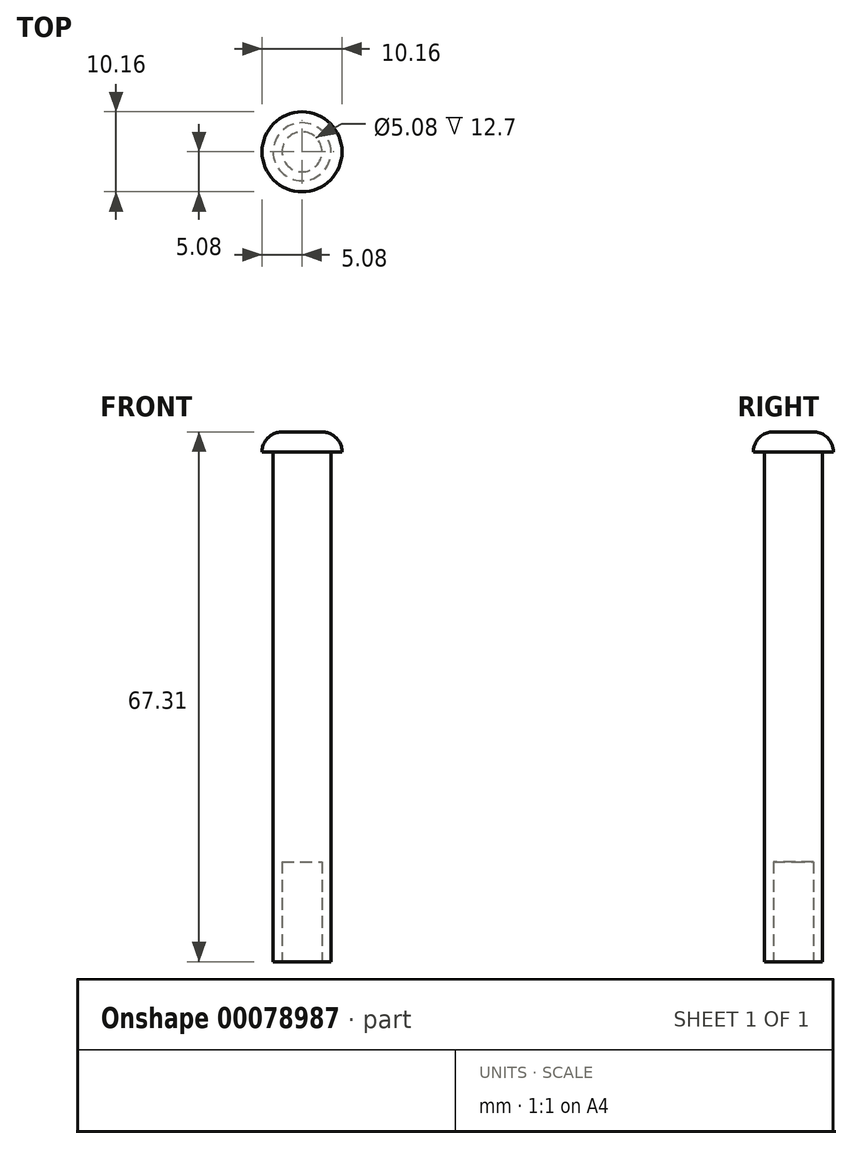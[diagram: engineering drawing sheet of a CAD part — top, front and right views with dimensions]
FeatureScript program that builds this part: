
annotation { "Feature Type Name" : "Feature", "Feature Type Description" : "" }
export const myFeature = defineFeature(function(context is Context, id is Id, definition is map)
    precondition{}
    {
        {
            var Q0;
            Q0=qCreatedBy(makeId("Top.planeOp"),FACE);
            var sketch = newSketch(context, id + "F0", { "sketchPlane" : qUnion([Q0])});
            skCircle(sketch, "E0", {"center": v(0, 0) * mm, "radius": 3.68 * mm});
            skSolve(sketch);
        }
        {
            var Q0;
            Q0 = qSketchRegion(id + "F0", true);
            extrude(context, id + "F1", {"entities" : qUnion([Q0]), "depth" : 64.77 * mm});
        }
        {
            var Q0;
            Q0=makeQuery(id+"F1.opExtrude","CAP_FACE",FACE,{"disambiguationData":[OSD([sQuery(id+"F0.wireOp",EDGE,"E0")])],"isStart":false});
            var sketch = newSketch(context, id + "F2", { "sketchPlane" : qUnion([Q0])});
            skCircle(sketch, "E1", {"center": v(0, 0) * mm, "radius": 5.08 * mm});
            skSolve(sketch);
        }
        {
            var Q0;
            Q0 = qSketchRegion(id + "F2", true);
            extrude(context, id + "F3", {"entities" : qUnion([Q0]), "operationType" : NewBodyOperationType.ADD, "depth" : 2.54 * mm});
        }
        {
            var Q0;
            Q0=makeQuery(id+"F3.opExtrude","CAP_EDGE",EDGE,{"disambiguationData":[OSD([sQuery(id+"F2.wireOp",EDGE,"E1")])],"isStart":false});
            fillet(context, id + "F4", {"entities" : qUnion([Q0]), "radius" : 2.54 * mm, "tangentPropagation" : true, "allowEdgeOverflow" : false});
        }
        {
            var Q0;
            Q0=makeQuery(id+"F1.opExtrude","CAP_FACE",FACE,{"disambiguationData":[OSD([sQuery(id+"F0.wireOp",EDGE,"E0")])],"isStart":true});
            var sketch = newSketch(context, id + "F5", { "sketchPlane" : qUnion([Q0])});
            skCircle(sketch, "E2", {"center": v(0, 0) * mm, "radius": 2.54 * mm});
            skSolve(sketch);
        }
        {
            var Q0;
            Q0 = qSketchRegion(id + "F5", true);
            extrude(context, id + "F6", {"entities" : qUnion([Q0]), "operationType" : NewBodyOperationType.REMOVE, "oppositeDirection" : true, "depth" : 12.7 * mm});
        }
    });
